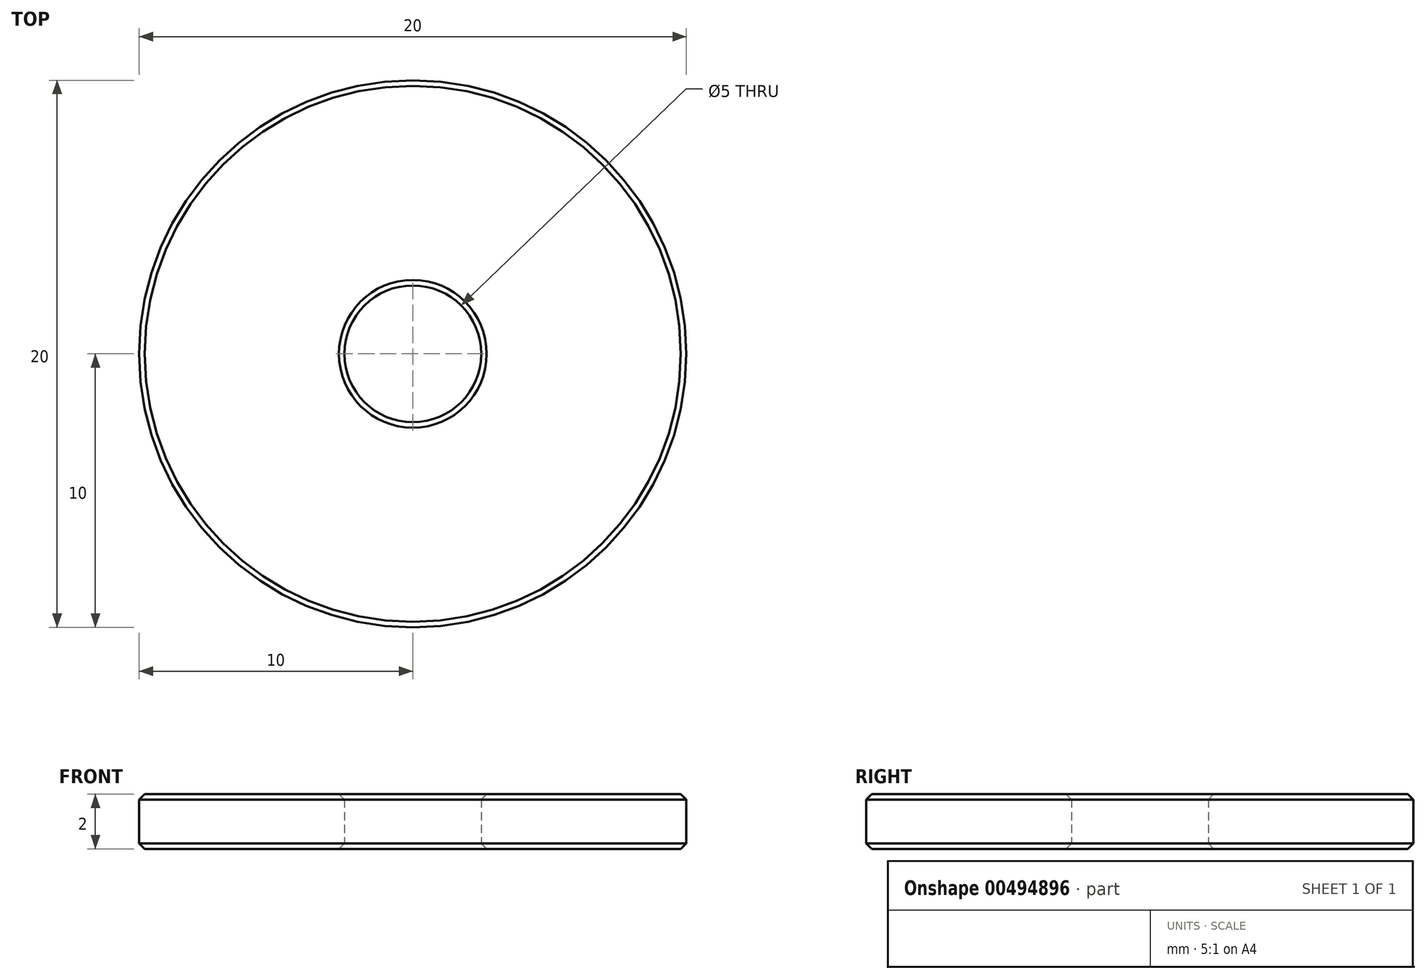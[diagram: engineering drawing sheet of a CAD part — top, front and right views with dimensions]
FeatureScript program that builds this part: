
annotation { "Feature Type Name" : "Feature", "Feature Type Description" : "" }
export const myFeature = defineFeature(function(context is Context, id is Id, definition is map)
    precondition{}
    {
        {
            var Q0;
            Q0=qCreatedBy(makeId("Top.planeOp"),FACE);
            var sketch = newSketch(context, id + "F0", { "sketchPlane" : qUnion([Q0])});
            skCircle(sketch, "E0", {"center": v(0, 0) * mm, "radius": 10 * mm});
            skCircle(sketch, "E1", {"center": v(0, 0) * mm, "radius": 2.5 * mm});
            skSolve(sketch);
        }
        {
            var Q0;
            Q0=qSketchRegion(id+"F0",true);
            extrude(context, id + "F1", {"entities" : qUnion([Q0]), "depth" : 2 * mm});
        }
        {
            var Q0;
            Q0=makeQuery(id+"F1.opExtrude","CAP_EDGE",EDGE,{"disambiguationData":[OSD([sQuery(id+"F0.wireOp",EDGE,"E0")])],"isStart":false});
            var Q1;
            Q1=makeQuery(id+"F1.opExtrude","CAP_EDGE",EDGE,{"disambiguationData":[OSD([sQuery(id+"F0.wireOp",EDGE,"E1")])],"isStart":false});
            var Q2;
            Q2=makeQuery(id+"F1.opExtrude","CAP_EDGE",EDGE,{"disambiguationData":[OSD([sQuery(id+"F0.wireOp",EDGE,"E0")])],"isStart":true});
            var Q3;
            Q3=makeQuery(id+"F1.opExtrude","CAP_EDGE",EDGE,{"disambiguationData":[OSD([sQuery(id+"F0.wireOp",EDGE,"E1")])],"isStart":true});
            chamfer(context, id + "F2", {"entities" : qUnion([Q0, Q1, Q2, Q3]), "width" : 0.2 * mm, "tangentPropagation" : true});
        }
    });
